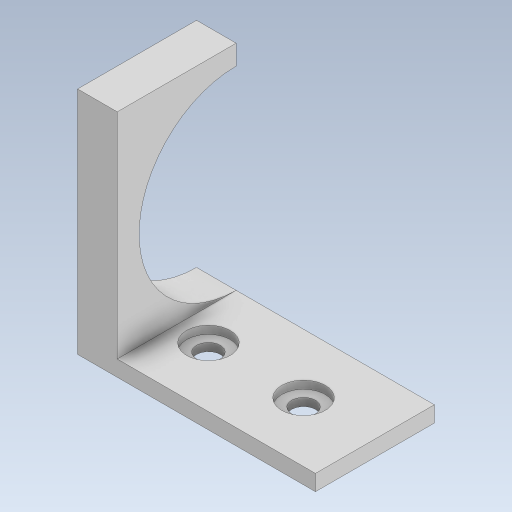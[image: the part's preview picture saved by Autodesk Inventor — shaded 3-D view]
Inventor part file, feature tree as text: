
AUTODESK INVENTOR PART (.ipt)
format: ipt  version: 2023.5 (Build 275446000, 446)  size: 294,400 bytes
history: native  units: in
note: dims shown in document units (in); Inventor stores cm internally (conversion verified against a paired STEP export)
features: extrude x5, sketch x3
ambient origin geometry x8: Origin, YZ Plane, XZ Plane, XY Plane, X Axis, Y Axis, Z Axis, Center Point
bodies: Solid1 (feature_tree)
feature tree (8):
  sketch  "Sketch1"  dims[d0=1.1811in d1=0.5906in]
  extrude  "Extrusion1"  Depth=0.5906in
  extrude  "Extrusion2"  Depth=0.0787in
  extrude  "Extrusion3"  Depth=0.2362in
  extrude  "Extrusion4"  Depth=0.0787in TaperAngle=0.0deg
  extrude  "Extrusion5"  Depth=1.1417in TaperAngle=0.0deg
  sketch  "Sketch2"  dims[d2=0.0787in d3=0.1181in]
  sketch  "Sketch3"  dims[d4=0.2165in d5=0.2362in d6=0.0787in d7=0.0in d8=1.1417in d9=0.0in d10=0.0394in d11=0.0in d13=0.0787in d14=0.0in d16=0.9646in d17=0.4823in d18=0.1181in d19=0.0in d15=0.0197in]
